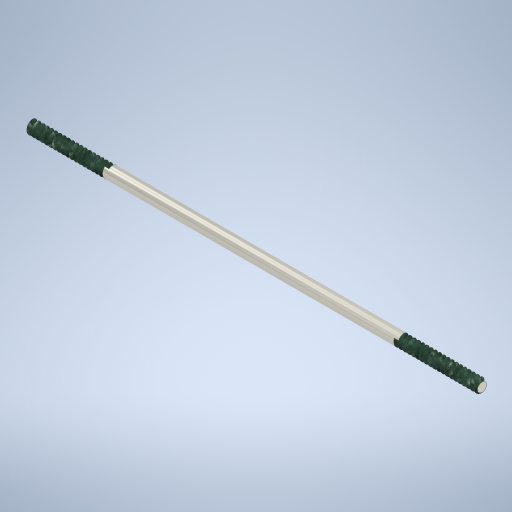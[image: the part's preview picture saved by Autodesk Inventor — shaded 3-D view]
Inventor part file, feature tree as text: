
AUTODESK INVENTOR PART (.ipt)
format: ipt  version: 2024 (Build 280153000, 153)  size: 431,104 bytes
history: native  units: mm
features: sketch x3, helix x2, extrude x1
ambient origin geometry x8: Origin, YZ Plane, XZ Plane, XY Plane, X Axis, Y Axis, Z Axis, Center Point
bodies: Solid1 (feature_tree)
feature tree (6):
  extrude  "Extrusion1"  Depth=1.7mm TaperAngle=0.0deg
  helix  "Coil1"  [1 undecoded]
  helix  "Coil2"  [1 undecoded]
  sketch  "Sketch1"  dims[d0=5.0mm d1=182.0mm d2=0.0mm d3=1.7mm d4=60.0deg]
  sketch  "Sketch2"  dims[d5=0.2mm]
  sketch  "Sketch3"  dims[d6=2.0mm d7=1.7mm d8=35.0mm d9=10.0mm d10=0.0mm d11=90.0deg d12=90.0deg d13=0.0mm d14=0.0mm d15=1.7mm d16=60.0deg d17=0.2mm d18=2.0mm d19=1.7mm d20=35.0mm d21=10.0mm d22=0.0mm d23=90.0deg d24=90.0deg d25=0.0mm d26=0.0mm]
note: 2 required parameter values undecoded (feature->parameter linkage not recoverable at this tier; creation-order binding heuristic only, values carry confidence <= 0.55)
